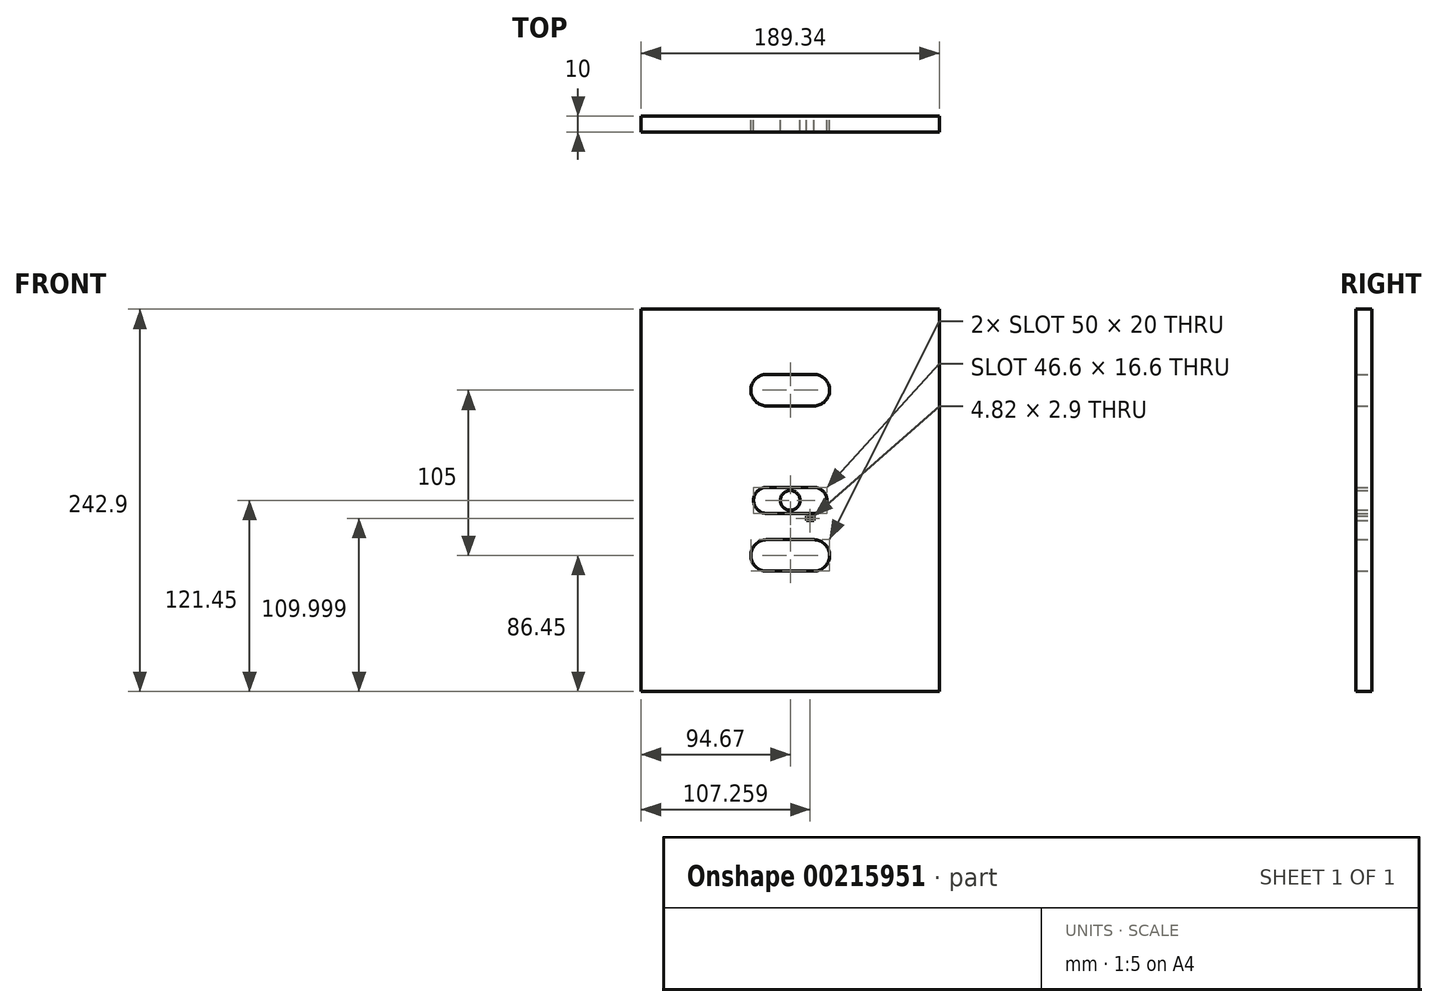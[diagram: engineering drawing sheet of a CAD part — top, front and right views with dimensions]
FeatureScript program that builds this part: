
annotation { "Feature Type Name" : "Feature", "Feature Type Description" : "" }
export const myFeature = defineFeature(function(context is Context, id is Id, definition is map)
    precondition{}
    {
        {
            var Q0;
            Q0=qCreatedBy(makeId("Front.planeOp"),FACE);
            var sketch = newSketch(context, id + "F0", { "sketchPlane" : qUnion([Q0])});
            skLineSegment(sketch, "E0.bottom", {"start": v(15, 10) * mm, "end": v(-15, 10) * mm});
            skLineSegment(sketch, "E0.top", {"start": v(15, -10) * mm, "end": v(-15, -10) * mm});
            skLineSegment(sketch, "E0.left", {"start": v(25, 0) * mm, "end": v(25, 0) * mm});
            skLineSegment(sketch, "E0.right", {"start": v(-25, 0) * mm, "end": v(-25, 0) * mm});
            skPoint(sketch, "E0.middle", {"position": v(0, 0) * mm});
            skPoint(sketch, "E1.visualSharp", {"position": v(-25, 10) * mm});
            skArc(sketch, "E1.filletArc", {"start": v(-15, 10) * mm, "mid": v(-22.07, 7.07) * mm, "end": v(-25, 0) * mm});
            skPoint(sketch, "E2.visualSharp", {"position": v(-25, -10) * mm});
            skArc(sketch, "E2.filletArc", {"start": v(-25, 0) * mm, "mid": v(-22.07, -7.07) * mm, "end": v(-15, -10) * mm});
            skPoint(sketch, "E3.visualSharp", {"position": v(25, 10) * mm});
            skArc(sketch, "E3.filletArc", {"start": v(25, 0) * mm, "mid": v(22.07, 7.07) * mm, "end": v(15, 10) * mm});
            skPoint(sketch, "E4.visualSharp", {"position": v(25, -10) * mm});
            skArc(sketch, "E4.filletArc", {"start": v(15, -10) * mm, "mid": v(22.07, -7.07) * mm, "end": v(25, 0) * mm});
            skLineSegment(sketch, "E5.bottom", {"start": v(15, 25) * mm, "end": v(-15, 25) * mm});
            skLineSegment(sketch, "E5.top", {"start": v(15, 45) * mm, "end": v(-15, 45) * mm});
            skLineSegment(sketch, "E5.left", {"start": v(25, 35) * mm, "end": v(25, 35) * mm});
            skLineSegment(sketch, "E5.right", {"start": v(-25, 35) * mm, "end": v(-25, 35) * mm});
            skPoint(sketch, "E5.middle", {"position": v(0, 35) * mm});
            skPoint(sketch, "E6.visualSharp", {"position": v(-25, 45) * mm});
            skArc(sketch, "E6.filletArc", {"start": v(-15, 45) * mm, "mid": v(-22.07, 42.07) * mm, "end": v(-25, 35) * mm});
            skPoint(sketch, "E7.visualSharp", {"position": v(-25, 25) * mm});
            skArc(sketch, "E7.filletArc", {"start": v(-25, 35) * mm, "mid": v(-22.07, 27.93) * mm, "end": v(-15, 25) * mm});
            skPoint(sketch, "E8.visualSharp", {"position": v(25, 25) * mm});
            skArc(sketch, "E8.filletArc", {"start": v(15, 25) * mm, "mid": v(22.07, 27.93) * mm, "end": v(25, 35) * mm});
            skPoint(sketch, "E9.visualSharp", {"position": v(25, 45) * mm});
            skArc(sketch, "E9.filletArc", {"start": v(25, 35) * mm, "mid": v(22.07, 42.07) * mm, "end": v(15, 45) * mm});
            skLineSegment(sketch, "E10.bottom", {"start": v(94.67, 121.45) * mm, "end": v(-94.67, 121.45) * mm});
            skLineSegment(sketch, "E10.top", {"start": v(94.67, -121.45) * mm, "end": v(-94.67, -121.45) * mm});
            skLineSegment(sketch, "E10.left", {"start": v(94.67, 121.45) * mm, "end": v(94.67, -121.45) * mm});
            skLineSegment(sketch, "E10.right", {"start": v(-94.67, 121.45) * mm, "end": v(-94.67, -121.45) * mm});
            skPoint(sketch, "E11.MirrorP", {"position": v(0, -35) * mm});
            skArc(sketch, "E12.MirrorCS", {"start": v(25, -35) * mm, "mid": v(22.07, -42.07) * mm, "end": v(15, -45) * mm});
            skArc(sketch, "E13.MirrorCS", {"start": v(15, -25) * mm, "mid": v(22.07, -27.93) * mm, "end": v(25, -35) * mm});
            skArc(sketch, "E14.MirrorCS", {"start": v(-25, -35) * mm, "mid": v(-22.07, -27.93) * mm, "end": v(-15, -25) * mm});
            skLineSegment(sketch, "E15.MirrorCS", {"start": v(25, -35) * mm, "end": v(25, -35) * mm});
            skPoint(sketch, "E16.MirrorP", {"position": v(25, -25) * mm});
            skArc(sketch, "E17.MirrorCS", {"start": v(-15, -45) * mm, "mid": v(-22.07, -42.07) * mm, "end": v(-25, -35) * mm});
            skLineSegment(sketch, "E18.MirrorCS", {"start": v(15, -45) * mm, "end": v(-15, -45) * mm});
            skLineSegment(sketch, "E19.MirrorCS", {"start": v(15, -25) * mm, "end": v(-15, -25) * mm});
            skPoint(sketch, "E20.MirrorP", {"position": v(-25, -25) * mm});
            skPoint(sketch, "E21.MirrorP", {"position": v(-25, -45) * mm});
            skPoint(sketch, "E22.MirrorP", {"position": v(25, -45) * mm});
            skLineSegment(sketch, "E23.MirrorCS", {"start": v(-25, -35) * mm, "end": v(-25, -35) * mm});
            skCircle(sketch, "E24", {"center": v(0, 0) * mm, "radius": 6.25 * mm});
            skArc(sketch, "E25.0", {"start": v(23.3, 0) * mm, "mid": v(20.87, 5.87) * mm, "end": v(15, 8.3) * mm});
            skArc(sketch, "E25.1", {"start": v(-15, 8.3) * mm, "mid": v(-20.87, 5.87) * mm, "end": v(-23.3, 0) * mm});
            skArc(sketch, "E25.2", {"start": v(-23.3, 0) * mm, "mid": v(-20.87, -5.87) * mm, "end": v(-15, -8.3) * mm});
            skLineSegment(sketch, "E25.3", {"start": v(15, 8.3) * mm, "end": v(-15, 8.3) * mm});
            skLineSegment(sketch, "E25.4", {"start": v(15, -8.3) * mm, "end": v(-15, -8.3) * mm});
            skArc(sketch, "E25.5", {"start": v(15, -8.3) * mm, "mid": v(20.87, -5.87) * mm, "end": v(23.3, 0) * mm});
            skPoint(sketch, "E26", {"position": v(-0.05, 52.5) * mm});
            skLineSegment(sketch, "E27", {"start": v(-0.05, 52.5) * mm, "end": v(-23.34, 52.5) * mm});
            skArc(sketch, "E28.MirrorCS", {"start": v(25, 70) * mm, "mid": v(22.07, 62.93) * mm, "end": v(15, 60) * mm});
            skArc(sketch, "E29.MirrorCS", {"start": v(15, 80) * mm, "mid": v(22.07, 77.07) * mm, "end": v(25, 70) * mm});
            skPoint(sketch, "E30.MirrorP", {"position": v(-25, 60) * mm});
            skPoint(sketch, "E31.MirrorP", {"position": v(25, 80) * mm});
            skLineSegment(sketch, "E32.MirrorCS", {"start": v(25, 70) * mm, "end": v(25, 70) * mm});
            skArc(sketch, "E33.MirrorCS", {"start": v(-15, 60) * mm, "mid": v(-22.07, 62.93) * mm, "end": v(-25, 70) * mm});
            skLineSegment(sketch, "E34.MirrorCS", {"start": v(-25, 70) * mm, "end": v(-25, 70) * mm});
            skPoint(sketch, "E35.MirrorP", {"position": v(25, 60) * mm});
            skArc(sketch, "E36.MirrorCS", {"start": v(-25, 70) * mm, "mid": v(-22.07, 77.07) * mm, "end": v(-15, 80) * mm});
            skPoint(sketch, "E37.MirrorP", {"position": v(-25, 80) * mm});
            skLineSegment(sketch, "E38.MirrorCS", {"start": v(15, 80) * mm, "end": v(-15, 80) * mm});
            skPoint(sketch, "E39.MirrorP", {"position": v(0, 70) * mm});
            skLineSegment(sketch, "E40.MirrorCS", {"start": v(15, 60) * mm, "end": v(-15, 60) * mm});
            skLineSegment(sketch, "E41.bottom", {"start": v(15, -10) * mm, "end": v(10.18, -10) * mm});
            skLineSegment(sketch, "E41.top", {"start": v(15, -12.9) * mm, "end": v(10.18, -12.9) * mm});
            skLineSegment(sketch, "E41.left", {"start": v(15, -10) * mm, "end": v(15, -12.9) * mm});
            skLineSegment(sketch, "E41.right", {"start": v(10.18, -10) * mm, "end": v(10.18, -12.9) * mm});
            skSolve(sketch);
        }
        {
            var Q0;
            Q0=makeQuery(id+"F0.imprint","IMPRINT",FACE,{"disambiguationData":[TD([[makeQuery(id+"F0.imprint","IMPRINT",EDGE,{"derivedFrom":sQuery(id+"F0.wireOp",EDGE,"E5.bottom")}),-1.0]])]});
            var Q1;
            Q1=makeQuery(id+"F0.imprint","IMPRINT",FACE,{"disambiguationData":[TD([[makeQuery(id+"F0.imprint","IMPRINT",EDGE,{"derivedFrom":sQuery(id+"F0.wireOp",EDGE,"E24")}),1.0]])]});
            var Q2;
            Q2=makeQuery(id+"F0.imprint","IMPRINT",FACE,{"disambiguationData":[TD([[makeQuery(id+"F0.imprint","IMPRINT",EDGE,{"derivedFrom":sQuery(id+"F0.wireOp",EDGE,"E0.bottom")}),1.0]])]});
            var Q3;
            Q3=makeQuery(id+"F0.imprint","IMPRINT",FACE,{"disambiguationData":[TD([[makeQuery(id+"F0.imprint","IMPRINT",EDGE,{"derivedFrom":sQuery(id+"F0.wireOp",EDGE,"E12.MirrorCS")}),-1.0]])]});
            extrude(context, id + "F1", {"entities" : qUnion([Q0, Q1, Q2, Q3]), "depth" : 10 * mm});
        }
    });
